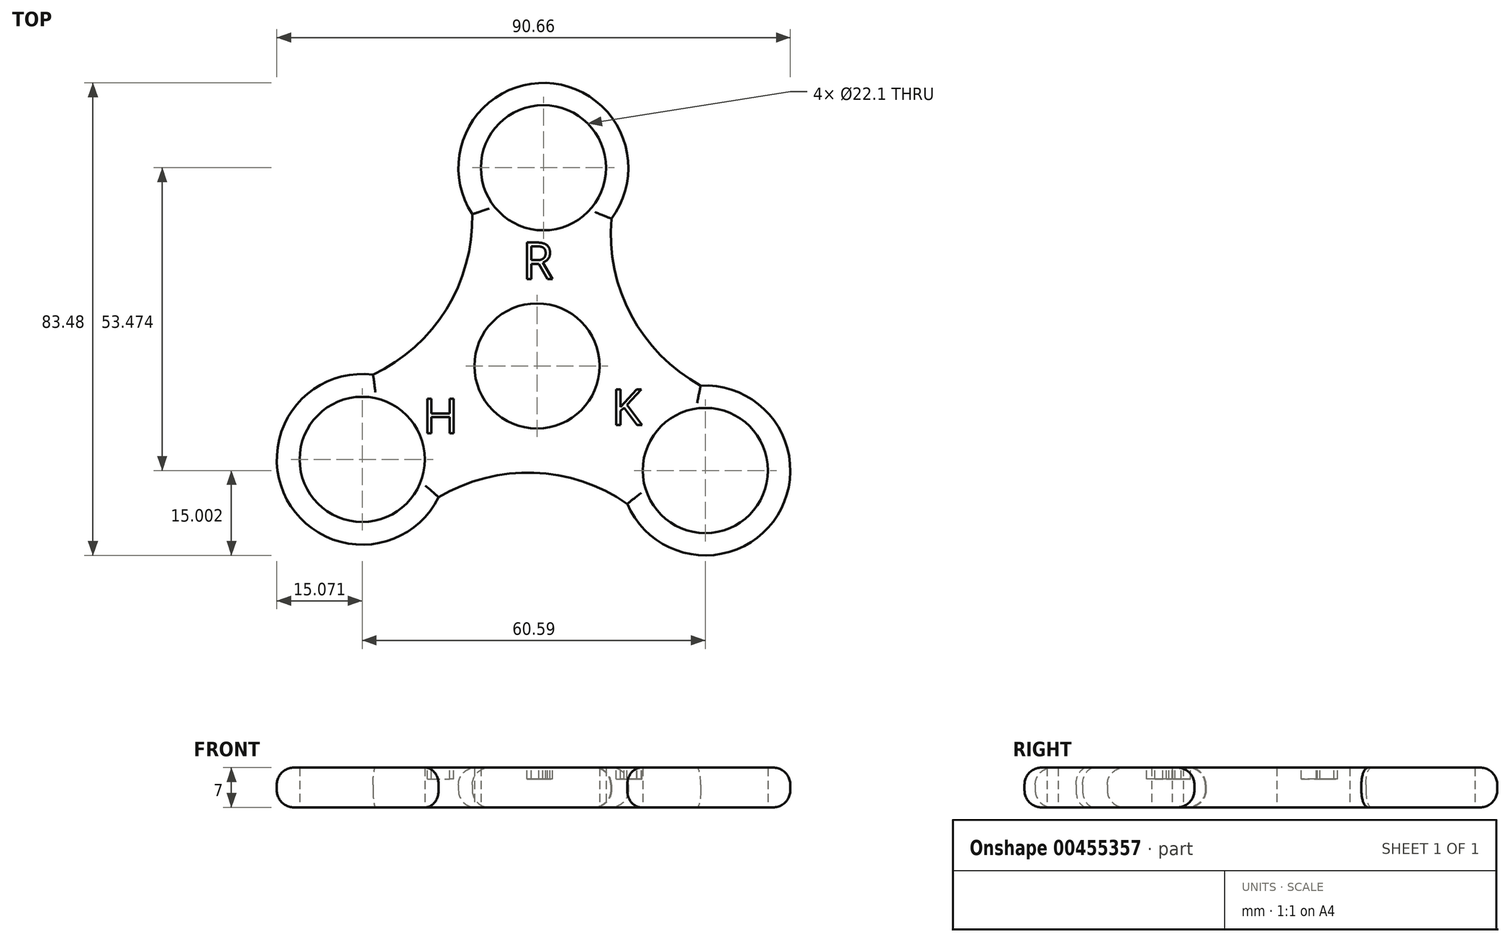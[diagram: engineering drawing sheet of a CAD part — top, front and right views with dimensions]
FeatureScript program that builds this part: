
annotation { "Feature Type Name" : "Feature", "Feature Type Description" : "" }
export const myFeature = defineFeature(function(context is Context, id is Id, definition is map)
    precondition{}
    {
        {
            var Q0;
            Q0=qCreatedBy(makeId("Top.planeOp"),FACE);
            var sketch = newSketch(context, id + "F0", { "sketchPlane" : qUnion([Q0])});
            skCircle(sketch, "E0", {"center": v(-1.14, 16.5) * mm, "radius": 11.05 * mm});
            skCircle(sketch, "E1", {"center": v(0, 51.5) * mm, "radius": 11.05 * mm});
            skCircle(sketch, "E2", {"center": v(-32, 0) * mm, "radius": 11.05 * mm});
            skCircle(sketch, "E3", {"center": v(28.6, -1.97) * mm, "radius": 11.05 * mm});
            skCircle(sketch, "E4", {"center": v(-1.14, 16.5) * mm, "radius": 15 * mm});
            skCircle(sketch, "E5", {"center": v(0, 51.5) * mm, "radius": 15 * mm});
            skCircle(sketch, "E6", {"center": v(-32, 0) * mm, "radius": 15.07 * mm});
            skCircle(sketch, "E7", {"center": v(28.6, -1.97) * mm, "radius": 15 * mm});
            skArc(sketch, "E8.MirrorCS", {"start": v(-25.4, -12.35) * mm, "mid": v(-1.75, -2.37) * mm, "end": v(21.2, -13.86) * mm});
            skLineSegment(sketch, "E9", {"start": v(-32, 0) * mm, "end": v(-1.14, 16.5) * mm});
            skLineSegment(sketch, "E10", {"start": v(-32, 0) * mm, "end": v(-25.4, -12.35) * mm});
            skLineSegment(sketch, "E11", {"start": v(-1.14, 16.5) * mm, "end": v(28.6, -1.97) * mm});
            skLineSegment(sketch, "E12", {"start": v(28.6, -1.97) * mm, "end": v(21.2, -13.86) * mm});
            skArc(sketch, "E13.MirrorCS", {"start": v(-38.6, 12.35) * mm, "mid": v(-17.18, 26.48) * mm, "end": v(-14, 51.94) * mm});
            skLineSegment(sketch, "E14.MirrorCS", {"start": v(-1.14, 16.5) * mm, "end": v(0, 51.49) * mm});
            skLineSegment(sketch, "E15.MirrorCS", {"start": v(0, 51.49) * mm, "end": v(-14, 51.94) * mm});
            skLineSegment(sketch, "E16.MirrorCS", {"start": v(-32, 0) * mm, "end": v(-38.6, 12.35) * mm});
            skArc(sketch, "E17.MirrorCS", {"start": v(14, 51.03) * mm, "mid": v(15.52, 25.42) * mm, "end": v(35.98, 9.92) * mm});
            skLineSegment(sketch, "E18.MirrorCS", {"start": v(28.6, -1.97) * mm, "end": v(35.98, 9.92) * mm});
            skSolve(sketch);
        }
        {
            var Q0;
            Q0 = qSketchRegion(id + "F0", true);
            var Q1;
            {var subQ0=sQuery(id+"F0.wireOp",EDGE,"E9");var subQ1=sQuery(id+"F0.wireOp",EDGE,"E0");var subQ2=makeQuery(id+"F0.imprint","INTERSECT",VERTEX,{"derivedFrom":[subQ1,subQ0]});Q1=makeQuery(id+"F0.imprint","IMPRINT",FACE,{"disambiguationData":[TD([[makeQuery(id+"F0.imprint","IMPRINT",EDGE,{"disambiguationData":[TD([[subQ2,1.0]])],"derivedFrom":subQ1}),-1.0]])]});}
            var Q2;
            {var subQ0=sQuery(id+"F0.wireOp",EDGE,"E9");var subQ1=sQuery(id+"F0.wireOp",EDGE,"E0");var subQ2=makeQuery(id+"F0.imprint","INTERSECT",VERTEX,{"derivedFrom":[subQ1,subQ0]});Q2=makeQuery(id+"F0.imprint","IMPRINT",FACE,{"disambiguationData":[TD([[makeQuery(id+"F0.imprint","IMPRINT",EDGE,{"disambiguationData":[TD([[subQ2,-1.0]])],"derivedFrom":subQ1}),-1.0]])]});}
            var Q3;
            {var subQ0=sQuery(id+"F0.wireOp",EDGE,"E14.MirrorCS");var subQ1=sQuery(id+"F0.wireOp",EDGE,"E0");var subQ2=makeQuery(id+"F0.imprint","INTERSECT",VERTEX,{"derivedFrom":[subQ1,subQ0]});Q3=makeQuery(id+"F0.imprint","IMPRINT",FACE,{"disambiguationData":[TD([[makeQuery(id+"F0.imprint","IMPRINT",EDGE,{"disambiguationData":[TD([[subQ2,1.0]])],"derivedFrom":subQ1}),-1.0]])]});}
            extrude(context, id + "F1", {"entities" : qUnion([Q0, Q1, Q2, Q3]), "depth" : 7 * mm});
        }
        {
            var Q0;
            Q0=makeQuery(id+"F1.opExtrude","CAP_EDGE",EDGE,{"disambiguationData":[OSD([sQuery(id+"F0.wireOp",EDGE,"E5")])],"isStart":true});
            var Q1;
            Q1=makeQuery(id+"F1.opExtrude","CAP_EDGE",EDGE,{"disambiguationData":[OSD([sQuery(id+"F0.wireOp",EDGE,"E13.MirrorCS")])],"isStart":true});
            var Q2;
            Q2=makeQuery(id+"F1.opExtrude","CAP_EDGE",EDGE,{"disambiguationData":[OSD([sQuery(id+"F0.wireOp",EDGE,"E6")])],"isStart":true});
            var Q3;
            Q3=makeQuery(id+"F1.opExtrude","CAP_EDGE",EDGE,{"disambiguationData":[OSD([sQuery(id+"F0.wireOp",EDGE,"E8.MirrorCS")])],"isStart":true});
            var Q4;
            Q4=makeQuery(id+"F1.opExtrude","CAP_EDGE",EDGE,{"disambiguationData":[OSD([sQuery(id+"F0.wireOp",EDGE,"E7")])],"isStart":true});
            var Q5;
            Q5=makeQuery(id+"F1.opExtrude","CAP_EDGE",EDGE,{"disambiguationData":[OSD([sQuery(id+"F0.wireOp",EDGE,"E17.MirrorCS")])],"isStart":true});
            fillet(context, id + "F2", {"entities" : qUnion([Q0, Q1, Q2, Q3, Q4, Q5]), "radius" : 3 * mm, "tangentPropagation" : true, "allowEdgeOverflow" : false});
        }
        {
            var Q0;
            Q0=makeQuery(id+"F1.opExtrude","CAP_EDGE",EDGE,{"disambiguationData":[OSD([sQuery(id+"F0.wireOp",EDGE,"E6")])],"isStart":false});
            var Q1;
            Q1=makeQuery(id+"F1.opExtrude","CAP_EDGE",EDGE,{"disambiguationData":[OSD([sQuery(id+"F0.wireOp",EDGE,"E13.MirrorCS")])],"isStart":false});
            var Q2;
            Q2=makeQuery(id+"F1.opExtrude","CAP_EDGE",EDGE,{"disambiguationData":[OSD([sQuery(id+"F0.wireOp",EDGE,"E5")])],"isStart":false});
            var Q3;
            Q3=makeQuery(id+"F1.opExtrude","CAP_EDGE",EDGE,{"disambiguationData":[OSD([sQuery(id+"F0.wireOp",EDGE,"E17.MirrorCS")])],"isStart":false});
            var Q4;
            Q4=makeQuery(id+"F1.opExtrude","CAP_EDGE",EDGE,{"disambiguationData":[OSD([sQuery(id+"F0.wireOp",EDGE,"E7")])],"isStart":false});
            var Q5;
            Q5=makeQuery(id+"F1.opExtrude","CAP_EDGE",EDGE,{"disambiguationData":[OSD([sQuery(id+"F0.wireOp",EDGE,"E8.MirrorCS")])],"isStart":false});
            fillet(context, id + "F3", {"entities" : qUnion([Q0, Q1, Q2, Q3, Q4, Q5]), "radius" : 3 * mm, "tangentPropagation" : true, "allowEdgeOverflow" : false});
        }
        {
            var Q0;
            Q0=makeQuery(id+"F1.opExtrude","CAP_FACE",FACE,{"disambiguationData":[OSD([sQuery(id+"F0.wireOp",EDGE,"E0"),sQuery(id+"F0.wireOp",EDGE,"E1"),sQuery(id+"F0.wireOp",EDGE,"E2"),sQuery(id+"F0.wireOp",EDGE,"E3"),sQuery(id+"F0.wireOp",EDGE,"E5"),sQuery(id+"F0.wireOp",EDGE,"E6"),sQuery(id+"F0.wireOp",EDGE,"E7"),sQuery(id+"F0.wireOp",EDGE,"E8.MirrorCS"),sQuery(id+"F0.wireOp",EDGE,"E13.MirrorCS"),sQuery(id+"F0.wireOp",EDGE,"E17.MirrorCS")])],"isStart":false});
            var sketch = newSketch(context, id + "F4", { "sketchPlane" : qUnion([Q0])});
            skText(sketch, "E19", { "text": "R", "fontName": "OpenSans-Regular.ttf"});
            skText(sketch, "E20", { "text": "H", "fontName": "OpenSans-Regular.ttf"});
            skText(sketch, "E21", { "text": "K", "fontName": "OpenSans-Regular.ttf"});
            const initialGuessF4  = {"E19": [-0.0038, 0.03187, 1, 0, 0.00649], "E20": [-0.0213, 0.0046, 1, 0, 0.00613], "E21": [0.01199, 0.00604, 1, 0, 0.00637]};
            skSetInitialGuess(sketch, initialGuessF4);
            skSolve(sketch);
        }
        {
            var Q0;
            Q0 = qSketchRegion(id + "F4", true);
            extrude(context, id + "F5", {"entities" : qUnion([Q0]), "operationType" : NewBodyOperationType.REMOVE, "oppositeDirection" : true, "depth" : 2 * mm});
        }
    });
